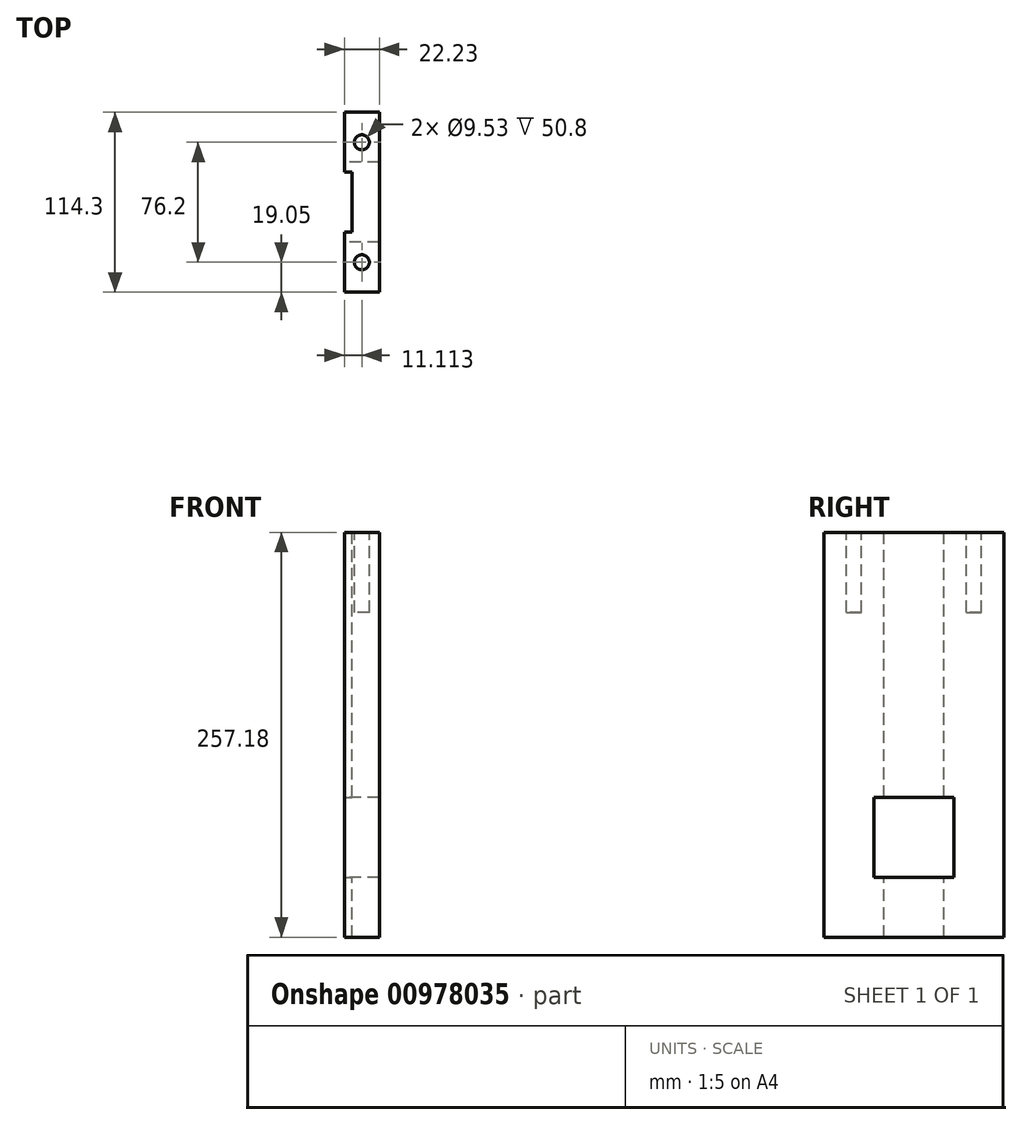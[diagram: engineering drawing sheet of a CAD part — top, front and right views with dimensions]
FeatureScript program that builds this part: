
annotation { "Feature Type Name" : "Feature", "Feature Type Description" : "" }
export const myFeature = defineFeature(function(context is Context, id is Id, definition is map)
    precondition{}
    {
        {
            var Q0;
            Q0=qCreatedBy(makeId("Right.planeOp"),FACE);
            var sketch = newSketch(context, id + "F0", { "sketchPlane" : qUnion([Q0])});
            skLineSegment(sketch, "E0", {"start": v(0, 128.59) * mm, "end": v(0, -128.59) * mm, "construction": true});
            skLineSegment(sketch, "E1", {"start": v(-57.15, 0) * mm, "end": v(57.15, 0) * mm, "construction": true});
            skLineSegment(sketch, "E2.bottom", {"start": v(-57.15, 128.59) * mm, "end": v(57.15, 128.59) * mm});
            skLineSegment(sketch, "E2.top", {"start": v(-57.15, -128.59) * mm, "end": v(57.15, -128.59) * mm});
            skLineSegment(sketch, "E2.left", {"start": v(-57.15, 128.59) * mm, "end": v(-57.15, -128.59) * mm});
            skLineSegment(sketch, "E2.right", {"start": v(57.15, 128.59) * mm, "end": v(57.15, -128.59) * mm});
            skLineSegment(sketch, "E3.bottom", {"start": v(-25.4, -39.69) * mm, "end": v(25.4, -39.69) * mm});
            skLineSegment(sketch, "E3.top", {"start": v(-25.4, -90.49) * mm, "end": v(25.4, -90.49) * mm});
            skLineSegment(sketch, "E3.left", {"start": v(-25.4, -39.69) * mm, "end": v(-25.4, -90.49) * mm});
            skLineSegment(sketch, "E3.right", {"start": v(25.4, -39.69) * mm, "end": v(25.4, -90.49) * mm});
            skSolve(sketch);
        }
        {
            var Q0;
            Q0=makeQuery(id+"F0.imprint","IMPRINT",FACE,{"disambiguationData":[TD([[makeQuery(id+"F0.imprint","IMPRINT",EDGE,{"derivedFrom":sQuery(id+"F0.wireOp",EDGE,"E2.bottom")}),-1.0]])]});
            extrude(context, id + "F1", {"entities" : qUnion([Q0]), "depth" : 22.22 * mm, "offsetDistance" : 25.4 * mm});
        }
        {
            var Q0;
            Q0=makeQuery(id+"F1.opExtrude","SWEPT_FACE",FACE,{"disambiguationData":[OSD([sQuery(id+"F0.wireOp",EDGE,"E2.bottom")])]});
            var sketch = newSketch(context, id + "F2", { "sketchPlane" : qUnion([Q0])});
            skLineSegment(sketch, "E4", {"start": v(0, 0) * mm, "end": v(22.23, 0) * mm, "construction": true});
            skLineSegment(sketch, "E5.0.0", {"start": v(0, 57.15) * mm, "end": v(0, -57.15) * mm});
            skLineSegment(sketch, "E5.0.1", {"start": v(0, -57.15) * mm, "end": v(22.23, -57.15) * mm});
            skLineSegment(sketch, "E5.0.2", {"start": v(22.23, -57.15) * mm, "end": v(22.23, 57.15) * mm});
            skLineSegment(sketch, "E5.0.3", {"start": v(22.23, 57.15) * mm, "end": v(0, 57.15) * mm});
            skLineSegment(sketch, "E6.bottom", {"start": v(0, -19.05) * mm, "end": v(4.76, -19.05) * mm});
            skLineSegment(sketch, "E6.top", {"start": v(0, 19.05) * mm, "end": v(4.76, 19.05) * mm});
            skLineSegment(sketch, "E6.left", {"start": v(0, -19.05) * mm, "end": v(0, 19.05) * mm});
            skLineSegment(sketch, "E6.right", {"start": v(4.76, -19.05) * mm, "end": v(4.76, 19.05) * mm});
            skSolve(sketch);
        }
        {
            var Q0;
            Q0=makeQuery(id+"F2.imprint","IMPRINT",FACE,{"disambiguationData":[TD([[makeQuery(id+"F2.imprint","IMPRINT",EDGE,{"derivedFrom":sQuery(id+"F2.wireOp",EDGE,"E6.bottom")}),1.0]])]});
            extrude(context, id + "F3", {"entities" : qUnion([Q0]), "operationType" : NewBodyOperationType.REMOVE, "endBound" : BoundingType.THROUGH_ALL, "oppositeDirection" : true, "depth" : 25.4 * mm, "offsetDistance" : 25.4 * mm});
        }
        {
            var Q0;
            Q0=makeQuery(id+"F1.opExtrude","SWEPT_FACE",FACE,{"disambiguationData":[OSD([sQuery(id+"F0.wireOp",EDGE,"E2.bottom")])]});
            var sketch = newSketch(context, id + "F4", { "sketchPlane" : qUnion([Q0])});
            skLineSegment(sketch, "E7", {"start": v(0, 0) * mm, "end": v(22.23, 0) * mm, "construction": true});
            skLineSegment(sketch, "E8", {"start": v(11.11, -57.15) * mm, "end": v(11.11, 57.15) * mm, "construction": true});
            skCircle(sketch, "E9", {"center": v(11.11, -38.1) * mm, "radius": 4.76 * mm});
            skCircle(sketch, "E10", {"center": v(11.11, 38.1) * mm, "radius": 4.76 * mm});
            skSolve(sketch);
        }
        {
            var Q0;
            Q0=makeQuery(id+"F4.imprint","IMPRINT",FACE,{"disambiguationData":[TD([[makeQuery(id+"F4.imprint","IMPRINT",EDGE,{"derivedFrom":sQuery(id+"F4.wireOp",EDGE,"E9")}),1.0]])]});
            var Q1;
            Q1=makeQuery(id+"F4.imprint","IMPRINT",FACE,{"disambiguationData":[TD([[makeQuery(id+"F4.imprint","IMPRINT",EDGE,{"derivedFrom":sQuery(id+"F4.wireOp",EDGE,"E10")}),1.0]])]});
            extrude(context, id + "F5", {"entities" : qUnion([Q0, Q1]), "operationType" : NewBodyOperationType.REMOVE, "oppositeDirection" : true, "depth" : 50.8 * mm, "offsetDistance" : 25.4 * mm});
        }
    });
